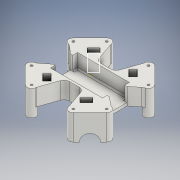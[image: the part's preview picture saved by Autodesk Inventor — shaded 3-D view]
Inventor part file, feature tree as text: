
AUTODESK INVENTOR PART (.ipt)
format: ipt  version: 2020 (Build 240168000, 168)  size: 543,232 bytes
history: native  units: mm
features: sketch x10, extrude x9, projected_geometry x6, fillet x3, other x1, mirror x1
ambient origin geometry x8: Origin, YZ Plane, XZ Plane, XY Plane, X Axis, Y Axis, Z Axis, Center Point
bodies: Body1 (feature_tree)
feature tree (30):
  other  "floor_v2.ipt"
  extrude  "Выдавливание2"  Depth=10.0mm
  extrude  "Выдавливание3"  Depth=12.0mm
  mirror  "Зеркальное отражение1"
  sketch  "Эскиз8"
  sketch  "Эскиз9"
  extrude  "Выдавливание4"  Depth=34.65mm TaperAngle=0.0deg
  extrude  "Выдавливание5"  Depth=20.3mm
  sketch  "Эскиз10"
  extrude  "Выдавливание6"  Depth=10.15mm TaperAngle=0.0deg
  sketch  "Эскиз11"
  extrude  "Выдавливание7"  Depth=9.0mm TaperAngle=0.0deg
  extrude  "Выдавливание10"  Depth=7.0mm TaperAngle=0.0deg
  fillet  "Сопряжение1"  Radius=70.45mm
  fillet  "Сопряжение2"  Radius=36.65mm
  extrude  "Выдавливание11"  Depth=76.45mm
  extrude  "Выдавливание12"  Depth=42.65mm
  fillet  "Сопряжение3"  Radius=3.225mm
  sketch  "Эскиз3"
  sketch  "Эскиз6"
  sketch  "Эскиз7"
  sketch  "Эскиз12"
  projected_geometry  "Спроецированная петля2"
  projected_geometry  "Спроецированная петля3"
  projected_geometry  "Спроецированная петля4"
  projected_geometry  "Спроецированная петля5"
  sketch  "Эскиз13"
  projected_geometry  "Спроецированная петля6"
  sketch  "Эскиз14"
  projected_geometry  "Спроецированная петля7"
